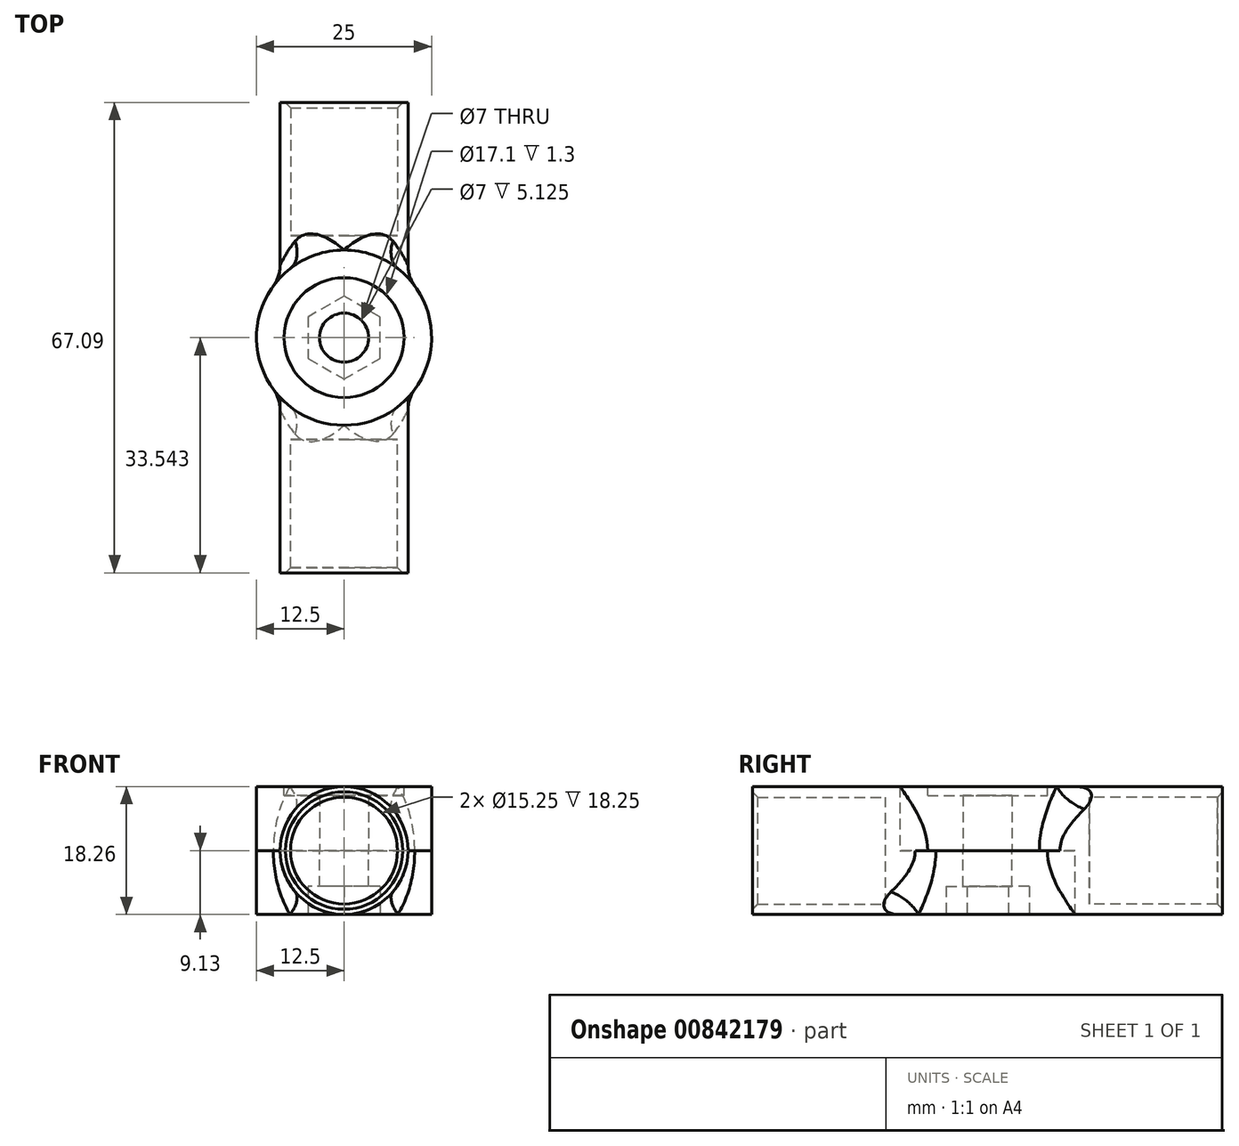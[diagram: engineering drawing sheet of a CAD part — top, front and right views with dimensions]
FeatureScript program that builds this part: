
annotation { "Feature Type Name" : "Feature", "Feature Type Description" : "" }
export const myFeature = defineFeature(function(context is Context, id is Id, definition is map)
    precondition{}
    {
        {
            var Q0;
            Q0=qCreatedBy(makeId("Front.planeOp"),FACE);
            var sketch = newSketch(context, id + "F0", { "sketchPlane" : qUnion([Q0])});
            skCircle(sketch, "E0", {"center": v(0, 0) * mm, "radius": 9.12 * mm});
            skCircle(sketch, "E1", {"center": v(0, 0) * mm, "radius": 7.62 * mm});
            skSolve(sketch);
        }
        {
            var Q0;
            Q0=qCreatedBy(makeId("Top.planeOp"),FACE);
            var sketch = newSketch(context, id + "F1", { "sketchPlane" : qUnion([Q0])});
            skCircle(sketch, "E2", {"center": v(0, 8.54) * mm, "radius": 12.5 * mm});
            skPoint(sketch, "E2.first.point", {"position": v(-9.12, 0) * mm});
            skPoint(sketch, "E2.second.point", {"position": v(9.12, 0) * mm});
            skPoint(sketch, "E2.third.point", {"position": v(-5.56, 19.74) * mm});
            skCircle(sketch, "E3", {"center": v(0, 8.54) * mm, "radius": 3.5 * mm});
            skLineSegment(sketch, "E4", {"start": v(-12.5, 8.54) * mm, "end": v(12.5, 8.54) * mm, "construction": true});
            skSolve(sketch);
        }
        {
            var Q0;
            Q0=makeQuery(id+"F1.imprint","IMPRINT",FACE,{"disambiguationData":[TD([[makeQuery(id+"F1.imprint","IMPRINT",EDGE,{"derivedFrom":sQuery(id+"F1.wireOp",EDGE,"E2")}),1.0]])]});
            extrude(context, id + "F2", {"entities" : qUnion([Q0]), "oppositeDirection" : true, "depth" : 9.12 * mm, "offsetDistance" : 25 * mm});
        }
        {
            var Q0;
            Q0=makeQuery(id+"F0.imprint","IMPRINT",FACE,{"disambiguationData":[TD([[makeQuery(id+"F0.imprint","IMPRINT",EDGE,{"derivedFrom":sQuery(id+"F0.wireOp",EDGE,"E0")}),1.0]])]});
            extrude(context, id + "F3", {"entities" : qUnion([Q0]), "operationType" : NewBodyOperationType.ADD, "depth" : 25 * mm, "offsetDistance" : 25 * mm});
        }
        {
            var Q0;
            Q0=makeQuery(id+"F0.imprint","IMPRINT",FACE,{"disambiguationData":[TD([[makeQuery(id+"F0.imprint","IMPRINT",EDGE,{"derivedFrom":sQuery(id+"F0.wireOp",EDGE,"E1")}),1.0]])]});
            extrude(context, id + "F4", {"entities" : qUnion([Q0]), "operationType" : NewBodyOperationType.ADD, "depth" : 6 * mm, "offsetDistance" : 25 * mm});
        }
        {
            var Q0;
            Q0=makeQuery(id+"F1.imprint","IMPRINT",FACE,{"disambiguationData":[TD([[makeQuery(id+"F1.imprint","IMPRINT",EDGE,{"derivedFrom":sQuery(id+"F1.wireOp",EDGE,"E2")}),1.0]])]});
            extrude(context, id + "F5", {"entities" : qUnion([Q0]), "operationType" : NewBodyOperationType.REMOVE, "depth" : 25 * mm, "offsetDistance" : 25 * mm});
        }
        {
            var Q0;
            Q0=makeQuery(id+"F2.opExtrude","SWEPT_BODY",BODY,{"disambiguationData":[OSD([sQuery(id+"F1.wireOp",EDGE,"E2"),sQuery(id+"F1.wireOp",EDGE,"E3")])]});
            var Q1;
            Q1=sQuery(id+"F1.wireOp",EDGE,"E4");
            transform(context, id + "F6", {"entities" : qUnion([Q0]), "transformType" : TransformType.ROTATION, "transformAxis" : qUnion([Q1]), "angle" : 180 * degree, "makeCopy" : true});
        }
        {
            var Q0;
            Q0=makeQuery(id+"F2.opExtrude","CAP_FACE",FACE,{"disambiguationData":[OSD([sQuery(id+"F1.wireOp",EDGE,"E2"),sQuery(id+"F1.wireOp",EDGE,"E3")])],"isStart":false});
            var sketch = newSketch(context, id + "F7", { "sketchPlane" : qUnion([Q0])});
            skCircle(sketch, "E5.cCircle", {"center": v(0, -8.54) * mm, "radius": 5.92 * mm, "construction": true});
            skLineSegment(sketch, "E5.0", {"start": v(0, -14.46) * mm, "end": v(-5.12, -11.5) * mm});
            skLineSegment(sketch, "E5.1", {"start": v(-5.12, -11.5) * mm, "end": v(-5.12, -5.58) * mm});
            skLineSegment(sketch, "E5.2", {"start": v(-5.13, -5.58) * mm, "end": v(0, -2.63) * mm});
            skLineSegment(sketch, "E5.3", {"start": v(0, -2.63) * mm, "end": v(5.12, -5.58) * mm});
            skLineSegment(sketch, "E5.4", {"start": v(5.12, -5.58) * mm, "end": v(5.13, -11.5) * mm});
            skLineSegment(sketch, "E5.5", {"start": v(5.12, -11.5) * mm, "end": v(0, -14.46) * mm});
            skSolve(sketch);
        }
        {
            var Q0;
            Q0=makeQuery(id+"F7.imprint","IMPRINT",FACE,{"disambiguationData":[TD([[makeQuery(id+"F7.imprint","IMPRINT",EDGE,{"derivedFrom":sQuery(id+"F7.wireOp",EDGE,"E5.0")}),-1.0]])]});
            extrude(context, id + "F8", {"entities" : qUnion([Q0]), "operationType" : NewBodyOperationType.REMOVE, "oppositeDirection" : true, "depth" : 4 * mm, "offsetDistance" : 25 * mm});
        }
        {
            var Q0;
            Q0=makeQuery(id+"F6.opPattern","COPY",FACE,{"derivedFrom":makeQuery(id+"F2.opExtrude","CAP_FACE",FACE,{"disambiguationData":[OSD([sQuery(id+"F1.wireOp",EDGE,"E2"),sQuery(id+"F1.wireOp",EDGE,"E3")])],"isStart":false}),"instanceName":"1"});
            var sketch = newSketch(context, id + "F9", { "sketchPlane" : qUnion([Q0])});
            skCircle(sketch, "E6", {"center": v(0, 8.54) * mm, "radius": 8.55 * mm});
            skSolve(sketch);
        }
        {
            var Q0;
            Q0=makeQuery(id+"F9.imprint","IMPRINT",FACE,{"disambiguationData":[TD([[makeQuery(id+"F9.imprint","IMPRINT",EDGE,{"derivedFrom":sQuery(id+"F9.wireOp",EDGE,"E6")}),1.0]])]});
            extrude(context, id + "F10", {"entities" : qUnion([Q0]), "operationType" : NewBodyOperationType.REMOVE, "oppositeDirection" : true, "depth" : 1.3 * mm, "offsetDistance" : 25 * mm});
        }
        {
            var Q0;
            Q0=makeQuery(id+"F6.opPattern","COPY",EDGE,{"derivedFrom":makeQuery(id+"F3.boolean.opBoolean","INTERSECT",EDGE,{"disambiguationData":[OD(1.0)],"derivedFrom":[makeQuery(id+"F2.opExtrude","SWEPT_FACE",FACE,{"disambiguationData":[OSD([sQuery(id+"F1.wireOp",EDGE,"E2")])]}),makeQuery(id+"F3.opExtrude","SWEPT_FACE",FACE,{"disambiguationData":[OSD([sQuery(id+"F0.wireOp",EDGE,"E0")])]})]}),"instanceName":"1"});
            var Q1;
            Q1=makeQuery(id+"F3.boolean.opBoolean","INTERSECT",EDGE,{"disambiguationData":[OD(0.0)],"derivedFrom":[makeQuery(id+"F2.opExtrude","SWEPT_FACE",FACE,{"disambiguationData":[OSD([sQuery(id+"F1.wireOp",EDGE,"E2")])]}),makeQuery(id+"F3.opExtrude","SWEPT_FACE",FACE,{"disambiguationData":[OSD([sQuery(id+"F0.wireOp",EDGE,"E0")])]})]});
            fillet(context, id + "F11", {"entities" : qUnion([Q0, Q1]), "tangentPropagation" : true, "radius" : 5 * mm, "defaultsChanged" : false, "vertexSettings" : [], "allowEdgeOverflow" : false});
        }
        {
            var Q0;
            Q0=makeQuery(id+"F6.opPattern","COPY",EDGE,{"derivedFrom":makeQuery(id+"F3.opExtrude","CAP_EDGE",EDGE,{"disambiguationData":[OSD([sQuery(id+"F0.wireOp",EDGE,"E1")])],"isStart":false}),"instanceName":"1"});
            var Q1;
            Q1=makeQuery(id+"F3.opExtrude","CAP_EDGE",EDGE,{"disambiguationData":[OSD([sQuery(id+"F0.wireOp",EDGE,"E1")])],"isStart":false});
            chamfer(context, id + "F12", {"entities" : qUnion([Q0, Q1]), "width" : 0.75 * mm, "tangentPropagation" : true});
        }
    });
